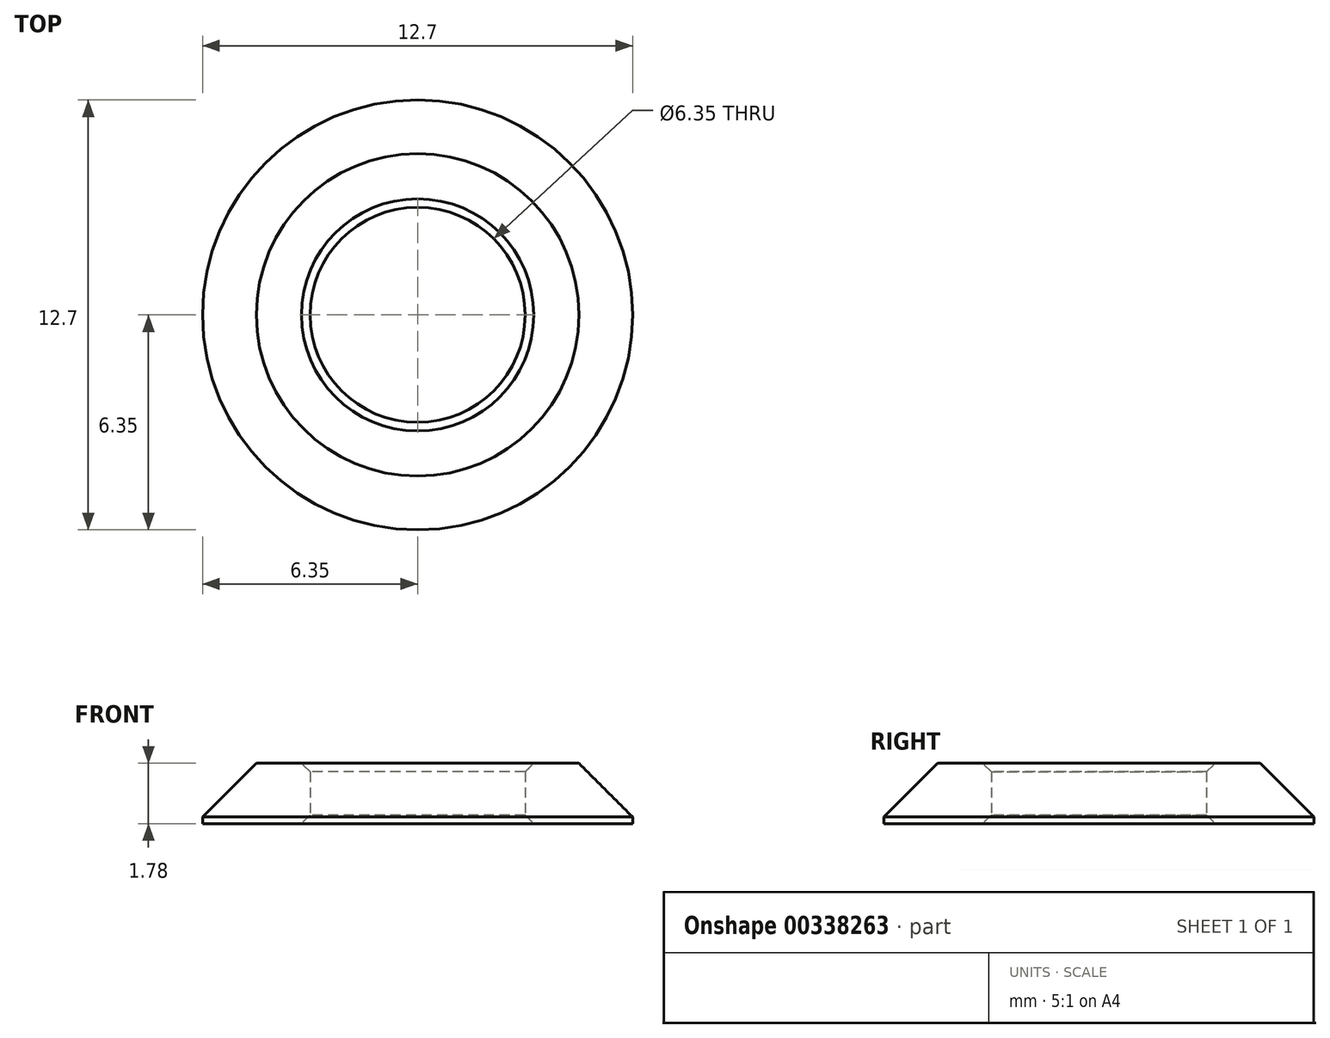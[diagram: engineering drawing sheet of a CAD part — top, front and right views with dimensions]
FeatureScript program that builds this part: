
annotation { "Feature Type Name" : "Feature", "Feature Type Description" : "" }
export const myFeature = defineFeature(function(context is Context, id is Id, definition is map)
    precondition{}
    {
        {
            var Q0;
            Q0=qCreatedBy(makeId("Top.planeOp"),FACE);
            var sketch = newSketch(context, id + "F0", { "sketchPlane" : qUnion([Q0])});
            skCircle(sketch, "E0", {"center": v(0, 0) * mm, "radius": 6.35 * mm});
            skCircle(sketch, "E1", {"center": v(0, 0) * mm, "radius": 3.18 * mm});
            skSolve(sketch);
        }
        {
            var Q0;
            Q0 = qSketchRegion(id + "F0", true);
            extrude(context, id + "F1", {"entities" : qUnion([Q0]), "depth" : (1.84 - (1 / 16)) * mm});
        }
        {
            var Q0;
            Q0=makeQuery(id+"F1.opExtrude","CAP_EDGE",EDGE,{"disambiguationData":[OSD([sQuery(id+"F0.wireOp",EDGE,"E0")])],"isStart":false});
            chamfer(context, id + "F2", {"entities" : qUnion([Q0]), "width" : 1.59 * mm, "tangentPropagation" : true});
        }
        {
            var Q0;
            Q0=makeQuery(id+"F1.opExtrude","CAP_EDGE",EDGE,{"disambiguationData":[OSD([sQuery(id+"F0.wireOp",EDGE,"E1")])],"isStart":false});
            var Q1;
            Q1=makeQuery(id+"F1.opExtrude","CAP_EDGE",EDGE,{"disambiguationData":[OSD([sQuery(id+"F0.wireOp",EDGE,"E1")])],"isStart":true});
            chamfer(context, id + "F3", {"entities" : qUnion([Q0, Q1]), "width" : 0.25 * mm, "tangentPropagation" : true});
        }
    });
